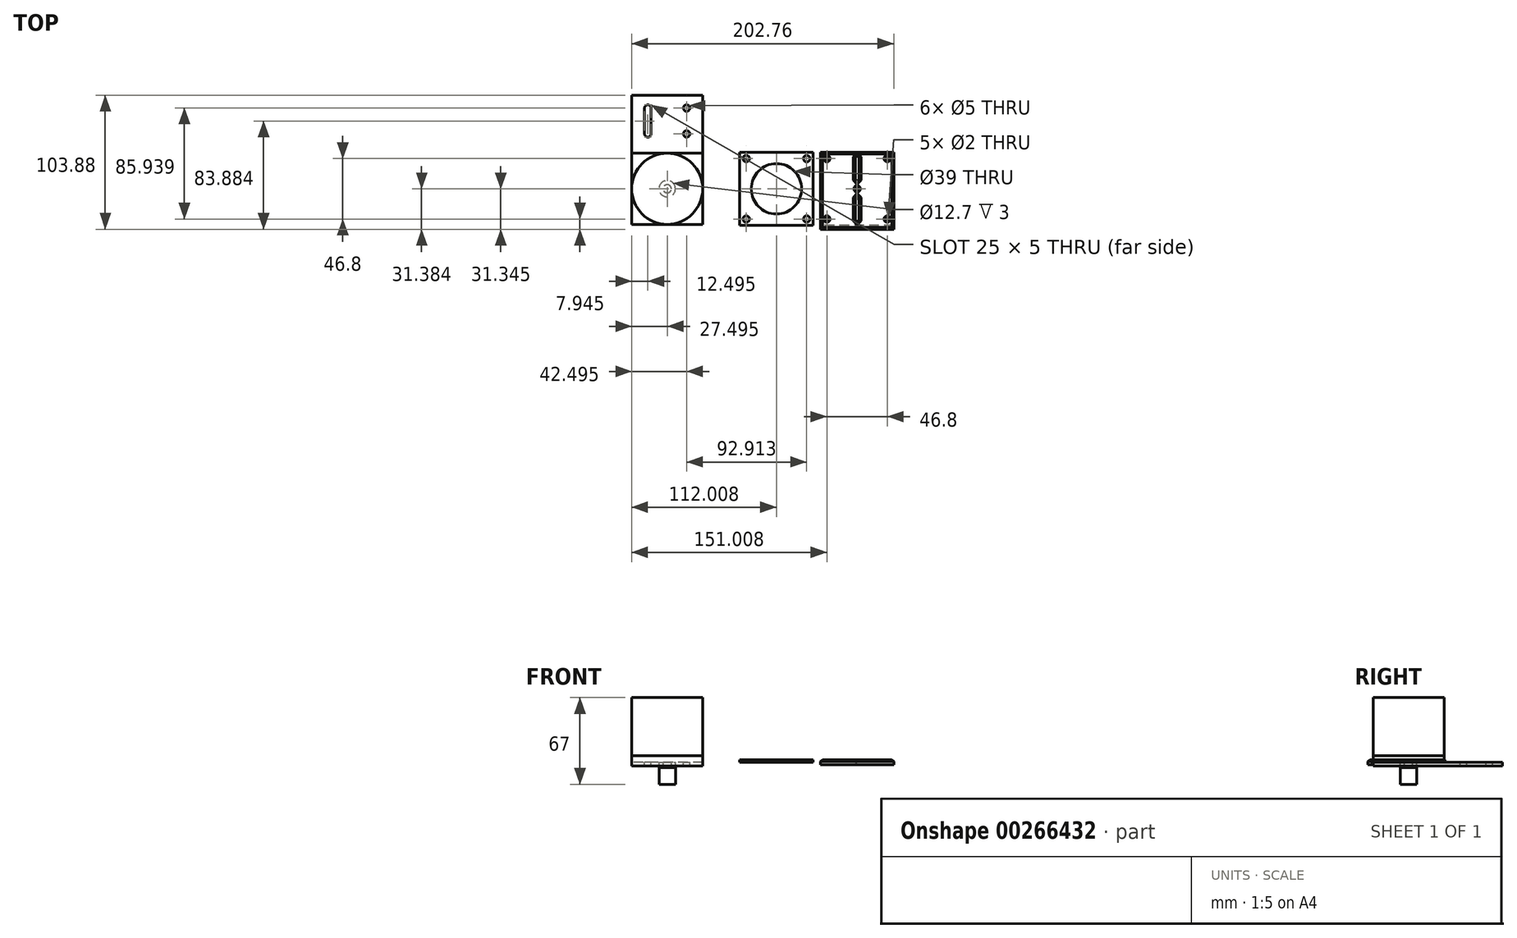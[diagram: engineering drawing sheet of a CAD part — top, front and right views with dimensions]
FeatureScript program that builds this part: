
annotation { "Feature Type Name" : "Feature", "Feature Type Description" : "" }
export const myFeature = defineFeature(function(context is Context, id is Id, definition is map)
    precondition{}
    {
        {
            var Q0;
            Q0=qCreatedBy(makeId("Top.planeOp"),FACE);
            var sketch = newSketch(context, id + "F0", { "sketchPlane" : qUnion([Q0])});
            skLineSegment(sketch, "E0.bottom", {"start": v(-15, -63.6) * mm, "end": v(-70, -63.6) * mm});
            skLineSegment(sketch, "E0.top", {"start": v(-15, -8.6) * mm, "end": v(-70, -8.6) * mm});
            skLineSegment(sketch, "E0.left", {"start": v(-15, -63.6) * mm, "end": v(-15, -8.6) * mm});
            skLineSegment(sketch, "E0.right", {"start": v(-70, -63.6) * mm, "end": v(-70, -8.6) * mm});
            skPoint(sketch, "E0.middle", {"position": v(-42.5, -36.1) * mm});
            skSolve(sketch);
        }
        {
            var Q0;
            Q0=makeQuery(id+"F0.imprint","IMPRINT",FACE,{"disambiguationData":[TD([[makeQuery(id+"F0.imprint","IMPRINT",EDGE,{"derivedFrom":sQuery(id+"F0.wireOp",EDGE,"E0.bottom")}),-1.0]])]});
            extrude(context, id + "F1", {"entities" : qUnion([Q0]), "depth" : 5 * mm});
        }
        {
            var Q0;
            Q0=makeQuery(id+"F1.opExtrude","CAP_FACE",FACE,{"disambiguationData":[OSD([sQuery(id+"F0.wireOp",EDGE,"E0.bottom"),sQuery(id+"F0.wireOp",EDGE,"E0.top"),sQuery(id+"F0.wireOp",EDGE,"E0.left"),sQuery(id+"F0.wireOp",EDGE,"E0.right")])],"isStart":false});
            var sketch = newSketch(context, id + "F2", { "sketchPlane" : qUnion([Q0])});
            skCircle(sketch, "E1", {"center": v(-42.5, -36.1) * mm, "radius": 27.5 * mm});
            skLineSegment(sketch, "E2", {"start": v(-42.5, -8.6) * mm, "end": v(-42.5, -36.1) * mm, "construction": true});
            skLineSegment(sketch, "E3", {"start": v(-42.5, -36.1) * mm, "end": v(-70, -36.1) * mm, "construction": true});
            skSolve(sketch);
        }
        {
            var Q0;
            Q0 = qSketchRegion(id + "F2", true);
            extrude(context, id + "F3", {"entities" : qUnion([Q0]), "operationType" : NewBodyOperationType.ADD, "depth" : 45 * mm});
        }
        {
            var Q0;
            Q0=makeQuery(id+"F1.opExtrude","CAP_FACE",FACE,{"disambiguationData":[OSD([sQuery(id+"F0.wireOp",EDGE,"E0.bottom"),sQuery(id+"F0.wireOp",EDGE,"E0.top"),sQuery(id+"F0.wireOp",EDGE,"E0.left"),sQuery(id+"F0.wireOp",EDGE,"E0.right")])],"isStart":true});
            var sketch = newSketch(context, id + "F4", { "sketchPlane" : qUnion([Q0])});
            skLineSegment(sketch, "E4", {"start": v(-42.5, 63.6) * mm, "end": v(-42.5, 36.1) * mm, "construction": true});
            skLineSegment(sketch, "E5", {"start": v(-42.5, 36.1) * mm, "end": v(-70, 36.1) * mm, "construction": true});
            skCircle(sketch, "E6", {"center": v(-42.5, 36.1) * mm, "radius": 3.18 * mm});
            skSolve(sketch);
        }
        {
            var Q0;
            Q0 = qSketchRegion(id + "F4", true);
            extrude(context, id + "F5", {"entities" : qUnion([Q0]), "operationType" : NewBodyOperationType.ADD, "depth" : 12 * mm});
        }
        {
            var Q0;
            Q0=makeQuery(id+"F1.opExtrude","CAP_FACE",FACE,{"disambiguationData":[OSD([sQuery(id+"F0.wireOp",EDGE,"E0.bottom"),sQuery(id+"F0.wireOp",EDGE,"E0.top"),sQuery(id+"F0.wireOp",EDGE,"E0.left"),sQuery(id+"F0.wireOp",EDGE,"E0.right")])],"isStart":true});
            var sketch = newSketch(context, id + "F6", { "sketchPlane" : qUnion([Q0])});
            skLineSegment(sketch, "E7.bottom", {"start": v(-70, 63.6) * mm, "end": v(-15, 63.6) * mm});
            skLineSegment(sketch, "E7.top", {"start": v(-70, -36.4) * mm, "end": v(-15, -36.4) * mm});
            skLineSegment(sketch, "E7.left", {"start": v(-70, 63.6) * mm, "end": v(-70, -36.4) * mm});
            skLineSegment(sketch, "E7.right", {"start": v(-15, 63.6) * mm, "end": v(-15, -36.4) * mm});
            skCircle(sketch, "E8", {"center": v(-42.5, 36.1) * mm, "radius": 6.35 * mm});
            skCircle(sketch, "E9", {"center": v(-27.5, -26.4) * mm, "radius": 2.5 * mm});
            skCircle(sketch, "E10", {"center": v(-27.5, -6.4) * mm, "radius": 2.5 * mm});
            skCircle(sketch, "E11", {"center": v(-57.5, -6.4) * mm, "radius": 2.5 * mm});
            skCircle(sketch, "E12", {"center": v(-57.5, -26.4) * mm, "radius": 2.5 * mm});
            skLineSegment(sketch, "E13", {"start": v(-42.5, -36.4) * mm, "end": v(-42.5, 8.6) * mm, "construction": true});
            skLineSegment(sketch, "E14", {"start": v(-55, -26.4) * mm, "end": v(-55, -6.4) * mm});
            skLineSegment(sketch, "E15", {"start": v(-60, -26.4) * mm, "end": v(-60, -6.4) * mm});
            skSolve(sketch);
        }
        {
            var Q0;
            Q0 = qSketchRegion(id + "F6", true);
            extrude(context, id + "F7", {"entities" : qUnion([Q0]), "operationType" : NewBodyOperationType.ADD, "depth" : 3 * mm});
        }
        {
            var Q0;
            Q0=makeQuery(id+"F5.opExtrude","CAP_FACE",FACE,{"disambiguationData":[OSD([sQuery(id+"F4.wireOp",EDGE,"E6")])],"isStart":false});
            var sketch = newSketch(context, id + "F8", { "sketchPlane" : qUnion([Q0])});
            skCircle(sketch, "E16", {"center": v(-42.5, 36.1) * mm, "radius": 6.35 * mm});
            skSolve(sketch);
        }
        {
            var Q0;
            Q0 = qSketchRegion(id + "F8", true);
            extrude(context, id + "F9", {"entities" : qUnion([Q0]), "operationType" : NewBodyOperationType.ADD, "oppositeDirection" : true, "depth" : 8 * mm, "hasSecondDirection" : true, "secondDirectionOppositeDirection" : false, "secondDirectionDepth" : 5 * mm});
        }
        {
            var Q0;
            Q0=qCreatedBy(makeId("Top.planeOp"),FACE);
            var sketch = newSketch(context, id + "F10", { "sketchPlane" : qUnion([Q0])});
            skLineSegment(sketch, "E17.bottom", {"start": v(13.67, -7.8) * mm, "end": v(70.37, -7.8) * mm});
            skLineSegment(sketch, "E17.top", {"start": v(13.67, -64.5) * mm, "end": v(70.37, -64.5) * mm});
            skLineSegment(sketch, "E17.left", {"start": v(13.67, -7.8) * mm, "end": v(13.67, -64.5) * mm});
            skLineSegment(sketch, "E17.right", {"start": v(70.37, -7.8) * mm, "end": v(70.37, -64.5) * mm});
            skLineSegment(sketch, "E18", {"start": v(13.67, -64.5) * mm, "end": v(70.37, -7.8) * mm, "construction": true});
            skPoint(sketch, "E19", {"position": v(42.02, -36.14) * mm});
            skCircle(sketch, "E20", {"center": v(42.02, -36.14) * mm, "radius": 19.5 * mm});
            skLineSegment(sketch, "E21.bottom", {"start": v(65.42, -59.54) * mm, "end": v(18.62, -59.54) * mm, "construction": true});
            skLineSegment(sketch, "E21.top", {"start": v(65.42, -12.74) * mm, "end": v(18.62, -12.74) * mm, "construction": true});
            skLineSegment(sketch, "E21.left", {"start": v(65.42, -59.54) * mm, "end": v(65.42, -12.74) * mm, "construction": true});
            skLineSegment(sketch, "E21.right", {"start": v(18.62, -59.54) * mm, "end": v(18.62, -12.74) * mm, "construction": true});
            skCircle(sketch, "E22", {"center": v(65.42, -59.54) * mm, "radius": 2.5 * mm});
            skCircle(sketch, "E23", {"center": v(65.42, -12.74) * mm, "radius": 2.5 * mm});
            skCircle(sketch, "E24", {"center": v(18.62, -12.74) * mm, "radius": 2.5 * mm});
            skCircle(sketch, "E25", {"center": v(18.62, -59.54) * mm, "radius": 2.5 * mm});
            skSolve(sketch);
        }
        {
            var Q0;
            Q0 = qSketchRegion(id + "F10", true);
            extrude(context, id + "F11", {"entities" : qUnion([Q0]), "depth" : 1.8 * mm});
        }
        {
            var Q0;
            Q0=qCreatedBy(makeId("Top.planeOp"),FACE);
            var sketch = newSketch(context, id + "F12", { "sketchPlane" : qUnion([Q0])});
            skLineSegment(sketch, "E26.bottom", {"start": v(13.67, -7.8) * mm, "end": v(70.37, -7.8) * mm});
            skLineSegment(sketch, "E26.top", {"start": v(13.67, -67.5) * mm, "end": v(70.37, -67.5) * mm});
            skLineSegment(sketch, "E26.left", {"start": v(13.67, -7.8) * mm, "end": v(13.67, -67.5) * mm});
            skLineSegment(sketch, "E26.right", {"start": v(70.37, -7.8) * mm, "end": v(70.37, -67.5) * mm});
            skCircle(sketch, "E27", {"center": v(42.02, -36.14) * mm, "radius": 1 * mm});
            skCircle(sketch, "E28", {"center": v(65.42, -12.74) * mm, "radius": 1 * mm});
            skCircle(sketch, "E29", {"center": v(65.42, -59.54) * mm, "radius": 1 * mm});
            skCircle(sketch, "E30", {"center": v(18.62, -12.74) * mm, "radius": 1 * mm});
            skCircle(sketch, "E31", {"center": v(18.62, -59.54) * mm, "radius": 1 * mm});
            skSolve(sketch);
        }
        {
            var Q0;
            Q0 = qSketchRegion(id + "F12", true);
            extrude(context, id + "F13", {"entities" : qUnion([Q0]), "depth" : 2 * mm});
        }
        {
            var Q0;
            Q0=makeQuery(id+"F13.opExtrude","SWEPT_BODY",BODY,{"disambiguationData":[OSD([sQuery(id+"F12.wireOp",EDGE,"E26.bottom"),sQuery(id+"F12.wireOp",EDGE,"E26.top"),sQuery(id+"F12.wireOp",EDGE,"E26.left"),sQuery(id+"F12.wireOp",EDGE,"E26.right"),sQuery(id+"F12.wireOp",EDGE,"E27"),sQuery(id+"F12.wireOp",EDGE,"E28"),sQuery(id+"F12.wireOp",EDGE,"E29"),sQuery(id+"F12.wireOp",EDGE,"E30"),sQuery(id+"F12.wireOp",EDGE,"E31")])]});
            transform(context, id + "F14", {"entities" : qUnion([Q0]), "transformType" : TransformType.TRANSLATION_3D, "dx" : 62.4 * mm, "dy" : 0 * mm, "dz" : 0 * mm, "makeCopy" : false});
        }
        {
            var Q0;
            Q0=makeQuery(id+"F13.opExtrude","CAP_FACE",FACE,{"disambiguationData":[OSD([sQuery(id+"F12.wireOp",EDGE,"E26.bottom"),sQuery(id+"F12.wireOp",EDGE,"E26.top"),sQuery(id+"F12.wireOp",EDGE,"E26.left"),sQuery(id+"F12.wireOp",EDGE,"E26.right"),sQuery(id+"F12.wireOp",EDGE,"E27"),sQuery(id+"F12.wireOp",EDGE,"E28"),sQuery(id+"F12.wireOp",EDGE,"E29"),sQuery(id+"F12.wireOp",EDGE,"E30"),sQuery(id+"F12.wireOp",EDGE,"E31")])],"isStart":true});
            var sketch = newSketch(context, id + "F15", { "sketchPlane" : qUnion([Q0])});
            skLineSegment(sketch, "E32.bottom", {"start": v(132.77, 67.5) * mm, "end": v(76.07, 67.5) * mm});
            skLineSegment(sketch, "E32.top", {"start": v(132.77, 64.5) * mm, "end": v(76.07, 64.5) * mm});
            skLineSegment(sketch, "E32.left", {"start": v(132.77, 67.5) * mm, "end": v(132.77, 64.5) * mm});
            skLineSegment(sketch, "E32.right", {"start": v(76.07, 67.5) * mm, "end": v(76.07, 64.5) * mm});
            skSolve(sketch);
        }
        {
            var Q0;
            Q0 = qSketchRegion(id + "F15", true);
            extrude(context, id + "F16", {"entities" : qUnion([Q0]), "operationType" : NewBodyOperationType.ADD, "depth" : 2 * mm});
        }
        {
            var Q0;
            Q0=makeQuery(id+"F13.opExtrude","CAP_FACE",FACE,{"disambiguationData":[OSD([sQuery(id+"F12.wireOp",EDGE,"E26.bottom"),sQuery(id+"F12.wireOp",EDGE,"E26.top"),sQuery(id+"F12.wireOp",EDGE,"E26.left"),sQuery(id+"F12.wireOp",EDGE,"E26.right"),sQuery(id+"F12.wireOp",EDGE,"E27"),sQuery(id+"F12.wireOp",EDGE,"E28"),sQuery(id+"F12.wireOp",EDGE,"E29"),sQuery(id+"F12.wireOp",EDGE,"E30"),sQuery(id+"F12.wireOp",EDGE,"E31")])],"isStart":false});
            var sketch = newSketch(context, id + "F17", { "sketchPlane" : qUnion([Q0])});
            skLineSegment(sketch, "E33", {"start": v(104.42, -36.14) * mm, "end": v(104.42, -67.5) * mm, "construction": true});
            skLineSegment(sketch, "E34.bottom", {"start": v(105.92, -61.82) * mm, "end": v(102.92, -61.82) * mm});
            skLineSegment(sketch, "E34.top", {"start": v(105.92, -41.82) * mm, "end": v(102.92, -41.82) * mm});
            skLineSegment(sketch, "E34.left", {"start": v(105.92, -61.82) * mm, "end": v(105.92, -41.82) * mm});
            skLineSegment(sketch, "E34.right", {"start": v(102.92, -61.82) * mm, "end": v(102.92, -41.82) * mm});
            skPoint(sketch, "E34.middle", {"position": v(104.42, -51.82) * mm});
            skLineSegment(sketch, "E35", {"start": v(104.42, -36.14) * mm, "end": v(126.4, -36.14) * mm, "construction": true});
            skLineSegment(sketch, "E36.MirrorCS", {"start": v(105.92, -30.47) * mm, "end": v(102.92, -30.47) * mm});
            skLineSegment(sketch, "E37.MirrorCS", {"start": v(105.92, -10.47) * mm, "end": v(102.92, -10.47) * mm});
            skLineSegment(sketch, "E38.MirrorCS", {"start": v(105.92, -10.47) * mm, "end": v(105.92, -30.47) * mm});
            skPoint(sketch, "E39.MirrorP", {"position": v(104.42, -20.47) * mm});
            skLineSegment(sketch, "E40.MirrorCS", {"start": v(102.92, -10.47) * mm, "end": v(102.92, -30.47) * mm});
            skSolve(sketch);
        }
        {
            var Q0;
            Q0 = qSketchRegion(id + "F17", true);
            extrude(context, id + "F18", {"entities" : qUnion([Q0]), "operationType" : NewBodyOperationType.REMOVE, "endBound" : BoundingType.THROUGH_ALL, "oppositeDirection" : true, "depth" : 25 * mm});
        }
        {
            var Q0;
            Q0=makeQuery(id+"F18.boolean.opBoolean","COPY",EDGE,{"derivedFrom":makeQuery(id+"F18.opExtrude","SWEPT_EDGE",EDGE,{"disambiguationData":[OSD([sQuery(id+"F17.wireOp",EDGE,"E37.MirrorCS"),sQuery(id+"F17.wireOp",EDGE,"E38.MirrorCS")])]})});
            var Q1;
            Q1=makeQuery(id+"F18.boolean.opBoolean","COPY",EDGE,{"derivedFrom":makeQuery(id+"F18.opExtrude","SWEPT_EDGE",EDGE,{"disambiguationData":[OSD([sQuery(id+"F17.wireOp",EDGE,"E34.top"),sQuery(id+"F17.wireOp",EDGE,"E34.left")])]})});
            var Q2;
            Q2=makeQuery(id+"F18.boolean.opBoolean","COPY",EDGE,{"derivedFrom":makeQuery(id+"F18.opExtrude","SWEPT_EDGE",EDGE,{"disambiguationData":[OSD([sQuery(id+"F17.wireOp",EDGE,"E37.MirrorCS"),sQuery(id+"F17.wireOp",EDGE,"E40.MirrorCS")])]})});
            var Q3;
            Q3=makeQuery(id+"F18.boolean.opBoolean","COPY",EDGE,{"derivedFrom":makeQuery(id+"F18.opExtrude","SWEPT_EDGE",EDGE,{"disambiguationData":[OSD([sQuery(id+"F17.wireOp",EDGE,"E34.top"),sQuery(id+"F17.wireOp",EDGE,"E34.right")])]})});
            var Q4;
            Q4=makeQuery(id+"F18.boolean.opBoolean","COPY",EDGE,{"derivedFrom":makeQuery(id+"F18.opExtrude","SWEPT_EDGE",EDGE,{"disambiguationData":[OSD([sQuery(id+"F17.wireOp",EDGE,"E36.MirrorCS"),sQuery(id+"F17.wireOp",EDGE,"E38.MirrorCS")])]})});
            var Q5;
            Q5=makeQuery(id+"F18.boolean.opBoolean","COPY",EDGE,{"derivedFrom":makeQuery(id+"F18.opExtrude","SWEPT_EDGE",EDGE,{"disambiguationData":[OSD([sQuery(id+"F17.wireOp",EDGE,"E34.bottom"),sQuery(id+"F17.wireOp",EDGE,"E34.left")])]})});
            var Q6;
            Q6=makeQuery(id+"F18.boolean.opBoolean","COPY",EDGE,{"derivedFrom":makeQuery(id+"F18.opExtrude","SWEPT_EDGE",EDGE,{"disambiguationData":[OSD([sQuery(id+"F17.wireOp",EDGE,"E36.MirrorCS"),sQuery(id+"F17.wireOp",EDGE,"E40.MirrorCS")])]})});
            var Q7;
            Q7=makeQuery(id+"F18.boolean.opBoolean","COPY",EDGE,{"derivedFrom":makeQuery(id+"F18.opExtrude","SWEPT_EDGE",EDGE,{"disambiguationData":[OSD([sQuery(id+"F17.wireOp",EDGE,"E34.bottom"),sQuery(id+"F17.wireOp",EDGE,"E34.right")])]})});
            chamfer(context, id + "F19", {"entities" : qUnion([Q0, Q1, Q2, Q3, Q4, Q5, Q6, Q7]), "width" : 1.5 * mm, "tangentPropagation" : true});
        }
        {
            var Q0;
            Q0=makeQuery(id+"F13.opExtrude","CAP_FACE",FACE,{"disambiguationData":[OSD([sQuery(id+"F12.wireOp",EDGE,"E26.bottom"),sQuery(id+"F12.wireOp",EDGE,"E26.top"),sQuery(id+"F12.wireOp",EDGE,"E26.left"),sQuery(id+"F12.wireOp",EDGE,"E26.right"),sQuery(id+"F12.wireOp",EDGE,"E27"),sQuery(id+"F12.wireOp",EDGE,"E28"),sQuery(id+"F12.wireOp",EDGE,"E29"),sQuery(id+"F12.wireOp",EDGE,"E30"),sQuery(id+"F12.wireOp",EDGE,"E31")])],"isStart":false});
            chamfer(context, id + "F20", {"entities" : qUnion([Q0]), "width" : 1.5 * mm, "tangentPropagation" : true});
        }
    });
